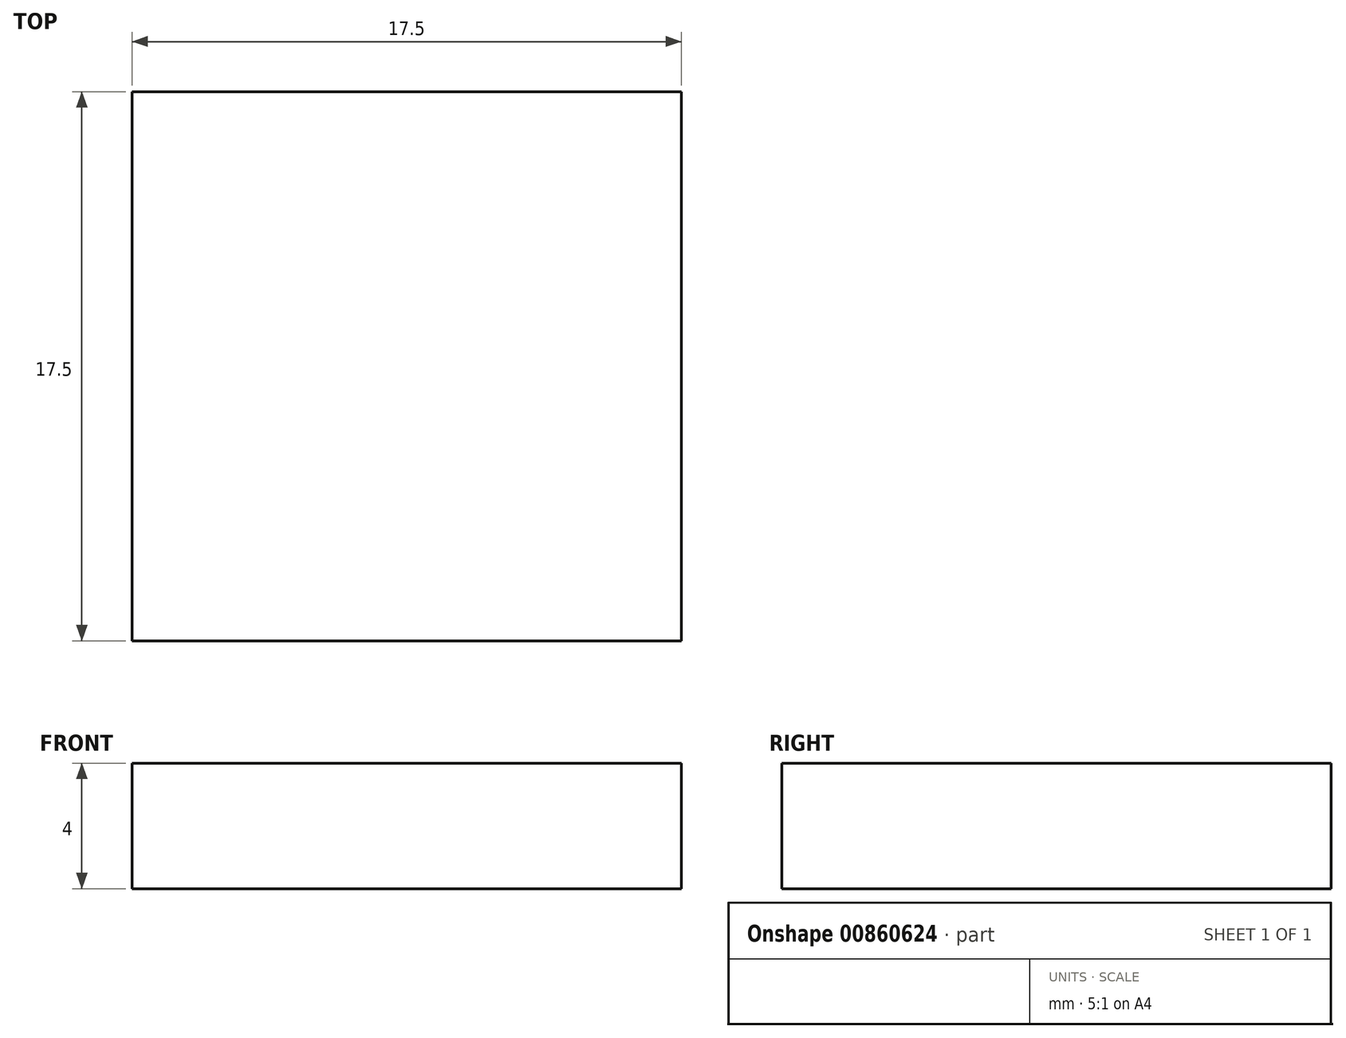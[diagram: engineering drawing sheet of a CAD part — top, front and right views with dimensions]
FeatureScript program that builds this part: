
annotation { "Feature Type Name" : "Feature", "Feature Type Description" : "" }
export const myFeature = defineFeature(function(context is Context, id is Id, definition is map)
    precondition{}
    {
        {
            var Q0;
            Q0=qCreatedBy(makeId("Right.planeOp"),FACE);
            var sketch = newSketch(context, id + "F0", { "sketchPlane" : qUnion([Q0])});
            skLineSegment(sketch, "E0.bottom", {"start": v(0, 0) * mm, "end": v(17.5, 0) * mm});
            skLineSegment(sketch, "E0.top", {"start": v(0, 4) * mm, "end": v(17.5, 4) * mm});
            skLineSegment(sketch, "E0.left", {"start": v(0, 0) * mm, "end": v(0, 4) * mm});
            skLineSegment(sketch, "E0.right", {"start": v(17.5, 0) * mm, "end": v(17.5, 4) * mm});
            skSolve(sketch);
        }
        {
            var Q0;
            Q0 = qSketchRegion(id + "F0", true);
            extrude(context, id + "F1", {"entities" : qUnion([Q0]), "depth" : 17.5 * mm, "offsetDistance" : 25 * mm});
        }
    });
